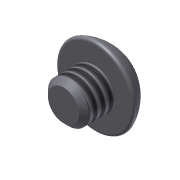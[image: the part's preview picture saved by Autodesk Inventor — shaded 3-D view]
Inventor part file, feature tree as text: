
AUTODESK INVENTOR PART (.ipt)
format: ipt  version: 2013 (Build 170138000, 138)  size: 133,632 bytes
history: native  units: in
note: dims shown in document units (in); Inventor stores cm internally (conversion verified against a paired STEP export)
features: sketch x3, extrude x2, revolve x1, chamfer x1, thread x1
ambient origin geometry x8: Origin, YZ Plane, XZ Plane, XY Plane, X Axis, Y Axis, Z Axis, Center Point
bodies: Solid1 (feature_tree)
feature tree (8):
  extrude  "Extrusion1"  Depth=0.125in TaperAngle=0.0deg
  revolve  "Revolution1"  [1 undecoded]
  extrude  "Extrusion2"  Depth=0.0938in
  chamfer  "Chamfer1"  Distance=0.0625in
  thread  "Thread1"  [1 undecoded]
  sketch  "Sketch1"  dims[d0=0.164in d1=0.125in d2=0.0in]
  sketch  "Sketch2"  dims[d3=0.087in d6=0.09in]
  sketch  "Sketch3"  dims[d7=90.0deg d8=0.0938in d9=0.0625in d10=0.0in d12=0.156in d13=0.02in d14=0.125in d15=45.0deg d16=1.0in d17=0.0in]
note: 2 required parameter values undecoded (feature->parameter linkage not recoverable at this tier; creation-order binding heuristic only, values carry confidence <= 0.55)